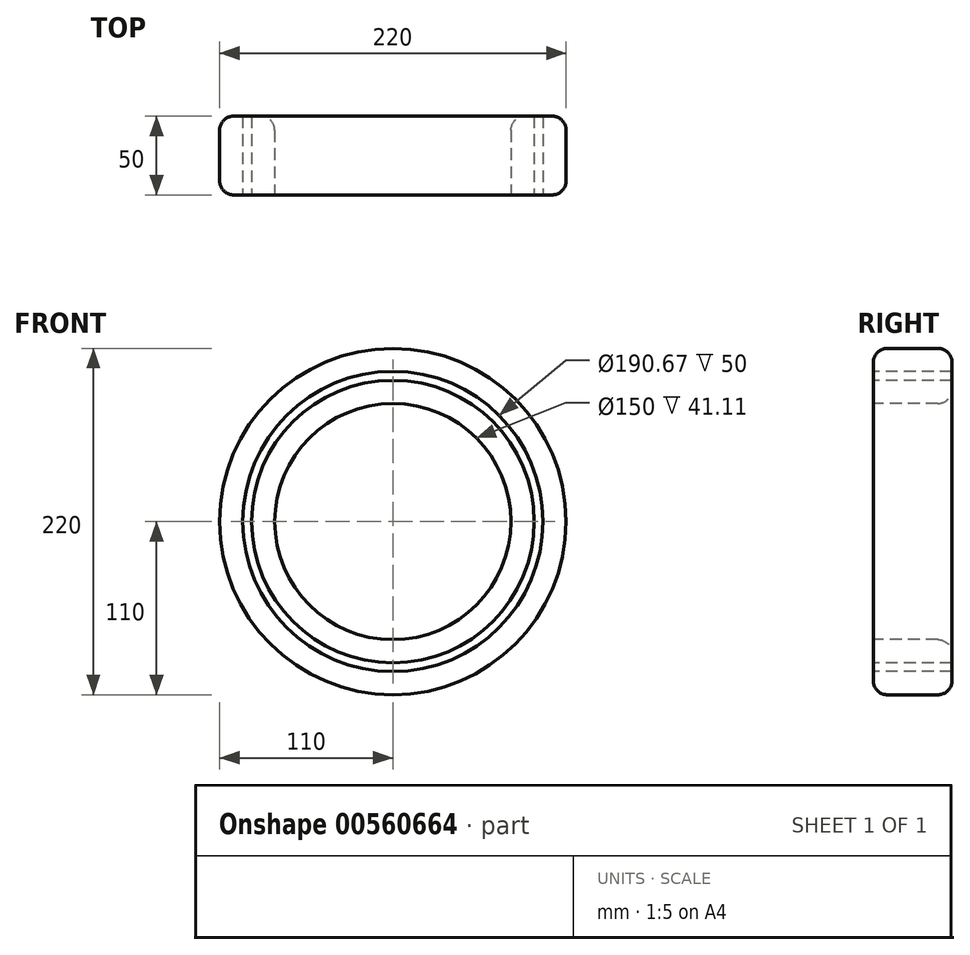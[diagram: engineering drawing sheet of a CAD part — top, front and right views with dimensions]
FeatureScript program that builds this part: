
annotation { "Feature Type Name" : "Feature", "Feature Type Description" : "" }
export const myFeature = defineFeature(function(context is Context, id is Id, definition is map)
    precondition{}
    {
        {
            var Q0;
            Q0=qCreatedBy(makeId("Front.planeOp"),FACE);
            var sketch = newSketch(context, id + "F0", { "sketchPlane" : qUnion([Q0])});
            skCircle(sketch, "E0", {"center": v(0, 0) * mm, "radius": 110 * mm});
            skSolve(sketch);
        }
        {
            var Q0;
            Q0=qSketchRegion(id+"F0",true);
            extrude(context, id + "F1", {"entities" : qUnion([Q0]), "depth" : 50 * mm, "offsetDistance" : 25.4 * mm});
        }
        {
            var Q0;
            Q0=makeQuery(id+"F1.opExtrude","CAP_FACE",FACE,{"disambiguationData":[OSD([sQuery(id+"F0.wireOp",EDGE,"E0")])],"isStart":false});
            var sketch = newSketch(context, id + "F2", { "sketchPlane" : qUnion([Q0])});
            skCircle(sketch, "E1", {"center": v(0, 0) * mm, "radius": 75 * mm});
            skSolve(sketch);
        }
        {
            var Q0;
            Q0=qSketchRegion(id+"F2",true);
            extrude(context, id + "F3", {"entities" : qUnion([Q0]), "operationType" : NewBodyOperationType.REMOVE, "endBound" : BoundingType.THROUGH_ALL, "oppositeDirection" : true, "depth" : 25.4 * mm, "offsetDistance" : 25.4 * mm});
        }
        {
            var Q0;
            Q0=qCreatedBy(makeId("Top.planeOp"),FACE);
            cPlane(context, id + "F4", {"entities" : qUnion([Q0]), "cplaneType" : CPlaneType.OFFSET, "offset" : 75.18 * mm, "width" : 152.4 * mm, "height" : 152.4 * mm});
        }
        {
            var Q0;
            Q0=qCreatedBy(id+"F4.planeOp",FACE);
            var sketch = newSketch(context, id + "F5", { "sketchPlane" : qUnion([Q0])});
            skCircle(sketch, "E2", {"center": v(-0.04, -25.17) * mm, "radius": 16.85 * mm});
            skSolve(sketch);
        }
        {
            var Q0;
            Q0=sQuery(id+"F5.wireOp",EDGE,"E2");
            extrude(context, id + "F6", {"bodyType" : ToolBodyType.SURFACE, "surfaceEntities" : qUnion([Q0]), "oppositeDirection" : true, "depth" : 151.38 * mm, "offsetDistance" : 25.4 * mm});
        }
        {
            var Q0;
            Q0=makeQuery(id+"F1.opExtrude","CAP_EDGE",EDGE,{"disambiguationData":[OSD([sQuery(id+"F0.wireOp",EDGE,"E0")])],"isStart":false});
            var Q1;
            Q1=makeQuery(id+"F3.boolean.opBoolean","COPY",EDGE,{"derivedFrom":makeQuery(id+"F3.opExtrude","CAP_EDGE",EDGE,{"disambiguationData":[OSD([sQuery(id+"F2.wireOp",EDGE,"E1")])],"isStart":true})});
            var Q2;
            Q2=makeQuery(id+"F1.opExtrude","CAP_EDGE",EDGE,{"disambiguationData":[OSD([sQuery(id+"F0.wireOp",EDGE,"E0")])],"isStart":true});
            var Q3;
            Q3=makeQuery(id+"F3.boolean.opBoolean","INTERSECT",EDGE,{"derivedFrom":[makeQuery(id+"F1.opExtrude","CAP_FACE",FACE,{"disambiguationData":[OSD([sQuery(id+"F0.wireOp",EDGE,"E0")])],"isStart":true}),makeQuery(id+"F3.opExtrude","SWEPT_FACE",FACE,{"disambiguationData":[OSD([sQuery(id+"F2.wireOp",EDGE,"E1")])]})]});
            fillet(context, id + "F7", {"entities" : qUnion([Q0, Q1, Q2, Q3]), "radius" : 8.9 * mm, "tangentPropagation" : true, "allowEdgeOverflow" : false});
        }
        {
            var Q0;
            Q0=makeQuery(id+"F1.opExtrude","CAP_FACE",FACE,{"disambiguationData":[OSD([sQuery(id+"F0.wireOp",EDGE,"E0")])],"isStart":false});
            var sketch = newSketch(context, id + "F8", { "sketchPlane" : qUnion([Q0])});
            skCircle(sketch, "E3", {"center": v(0, 0) * mm, "radius": 89.74 * mm});
            skCircle(sketch, "E4", {"center": v(0, 0) * mm, "radius": 95.33 * mm});
            skSolve(sketch);
        }
        {
            var Q0;
            Q0=makeQuery(id+"F8.imprint","IMPRINT",FACE,{"disambiguationData":[TD([[makeQuery(id+"F8.imprint","IMPRINT",EDGE,{"derivedFrom":sQuery(id+"F8.wireOp",EDGE,"E3")}),-1.0]])]});
            extrude(context, id + "F9", {"entities" : qUnion([Q0]), "operationType" : NewBodyOperationType.REMOVE, "endBound" : BoundingType.THROUGH_ALL, "oppositeDirection" : true, "depth" : 4.57 * mm, "offsetDistance" : 25.4 * mm});
        }
    });
